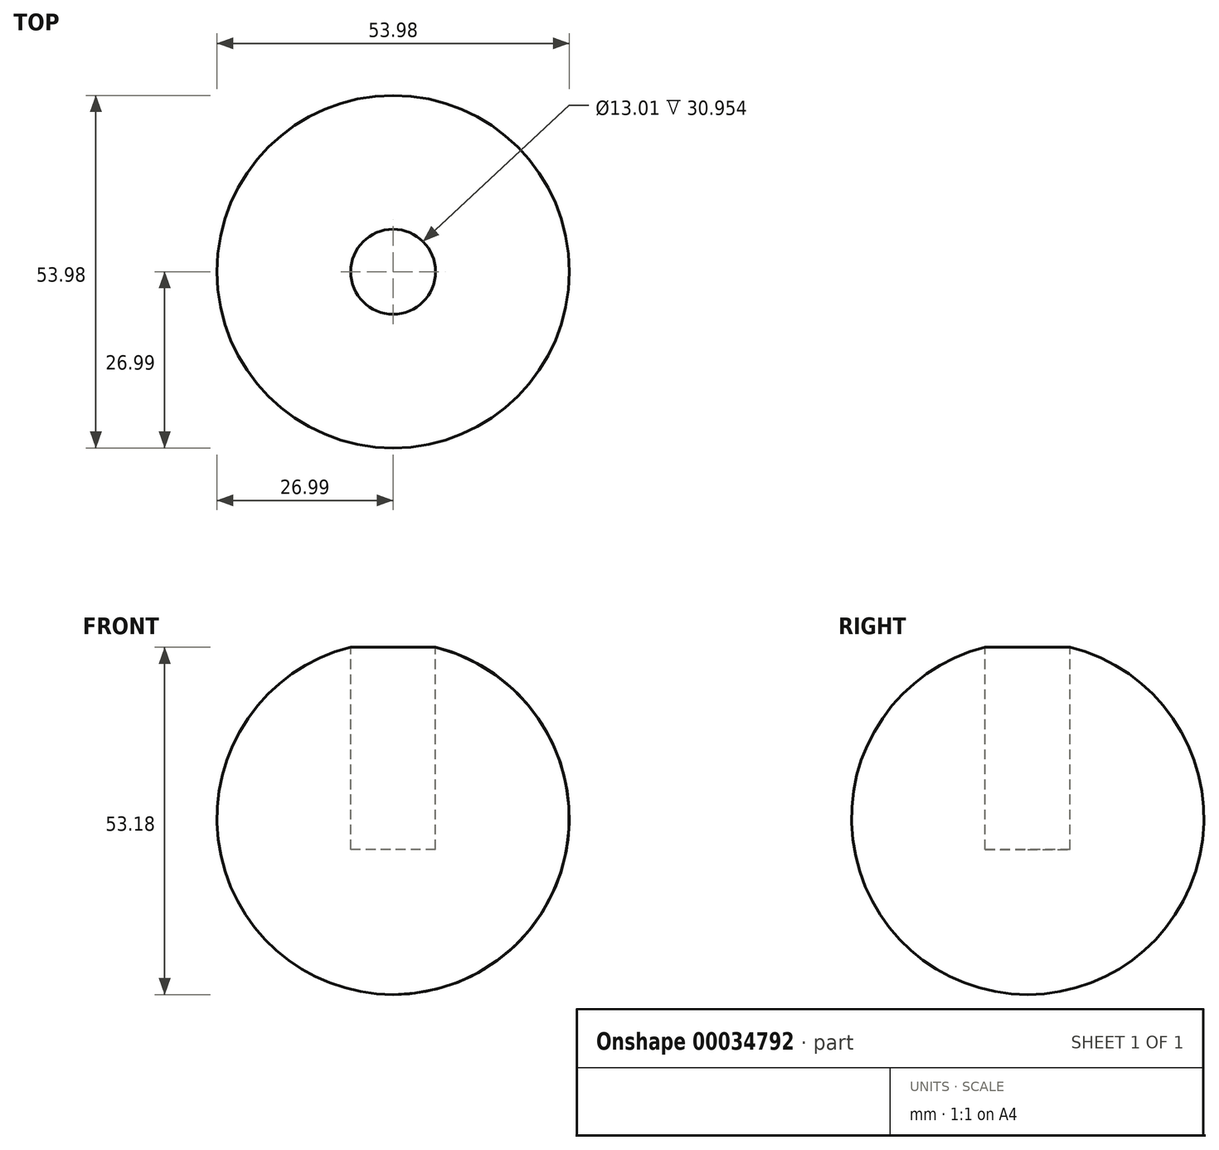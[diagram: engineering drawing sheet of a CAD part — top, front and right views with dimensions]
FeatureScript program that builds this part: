
annotation { "Feature Type Name" : "Feature", "Feature Type Description" : "" }
export const myFeature = defineFeature(function(context is Context, id is Id, definition is map)
    precondition{}
    {
        {
            var Q0;
            Q0=qCreatedBy(makeId("Top.planeOp"),FACE);
            var sketch = newSketch(context, id + "F0", { "sketchPlane" : qUnion([Q0])});
            skCircle(sketch, "E0", {"center": v(0, 0) * mm, "radius": 26.99 * mm});
            skSolve(sketch);
        }
        {
            var Q0;
            Q0=makeQuery(id+"F0.imprint","IMPRINT",FACE,{"disambiguationData":[TD([[makeQuery(id+"F0.imprint","IMPRINT",EDGE,{"derivedFrom":sQuery(id+"F0.wireOp",EDGE,"E0")}),1.0]])]});
            extrude(context, id + "F1", {"entities" : qUnion([Q0]), "depth" : 26.99 * mm, "hasSecondDirection" : true, "secondDirectionOppositeDirection" : true, "secondDirectionDepth" : 26.99 * mm});
        }
        {
            var Q0;
            Q0=makeQuery(id+"F1.opExtrude","CAP_FACE",FACE,{"disambiguationData":[OSD([sQuery(id+"F0.wireOp",EDGE,"E0")])],"isStart":false});
            var sketch = newSketch(context, id + "F2", { "sketchPlane" : qUnion([Q0])});
            skCircle(sketch, "E1.0", {"center": v(0, 0) * mm, "radius": 26.99 * mm});
            skCircle(sketch, "E2", {"center": v(0, 0) * mm, "radius": 6.5 * mm});
            skSolve(sketch);
        }
        {
            var Q0;
            Q0=makeQuery(id+"F1.opExtrude","CAP_EDGE",EDGE,{"disambiguationData":[OSD([sQuery(id+"F0.wireOp",EDGE,"E0")])],"isStart":false});
            var Q1;
            Q1=makeQuery(id+"F1.opExtrude","CAP_EDGE",EDGE,{"disambiguationData":[OSD([sQuery(id+"F0.wireOp",EDGE,"E0")])],"isStart":true});
            fillet(context, id + "F3", {"entities" : qUnion([Q0, Q1]), "radius" : 26.99 * mm, "tangentPropagation" : true, "allowEdgeOverflow" : false});
        }
        {
            var Q0;
            Q0=makeQuery(id+"F2.imprint","IMPRINT",FACE,{"disambiguationData":[TD([[makeQuery(id+"F2.imprint","IMPRINT",EDGE,{"derivedFrom":sQuery(id+"F2.wireOp",EDGE,"E2")}),1.0]])]});
            extrude(context, id + "F4", {"entities" : qUnion([Q0]), "operationType" : NewBodyOperationType.REMOVE, "oppositeDirection" : true, "depth" : 31.75 * mm});
        }
    });
